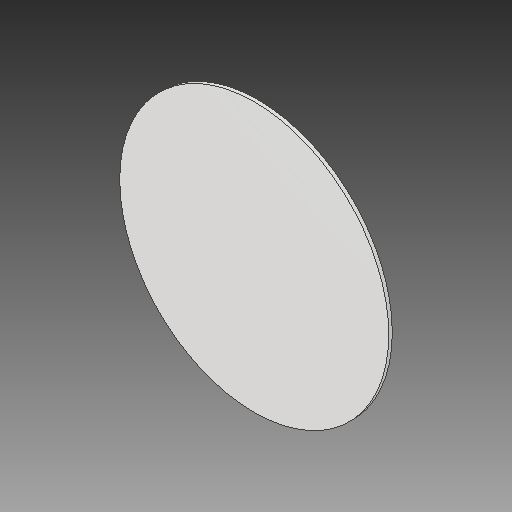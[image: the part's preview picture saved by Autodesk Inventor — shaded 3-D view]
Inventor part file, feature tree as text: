
AUTODESK INVENTOR PART (.ipt)
format: ipt  version: 2019 (Build 230136000, 136)  size: 92,160 bytes
history: native  units: in
note: dims shown in document units (in); Inventor stores cm internally (conversion verified against a paired STEP export)
features: other x3, extrude x1, sketch x1, reference x1
ambient origin geometry x8: Origin, YZ Plane, XZ Plane, XY Plane, X Axis, Y Axis, Z Axis, Center Point
bodies: Solid1 (feature_tree)
feature tree (6):
  extrude  "Extrusion1"  Depth=0.1in TaperAngle=0.0deg
  sketch  "Sketch1"  dims[d0=7.5in d1=0.1in d2=0.0in]
  reference  "Reference1"
  other  "<userpath>\Desktop\Roombotics\UpperLevel.iam"
  other  "UpperLevel.iam"
  other  "Stove:1"
